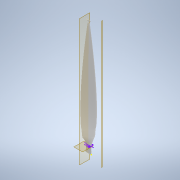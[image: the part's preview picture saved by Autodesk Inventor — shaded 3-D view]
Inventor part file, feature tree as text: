
AUTODESK INVENTOR PART (.ipt)
format: ipt  version: 2022 (Build 260153000, 153)  size: 1,145,856 bytes
history: native  units: mm
features: sketch x6, plane x3, loft x1, sweep x1
ambient origin geometry x8: Origin, YZ Plane, XZ Plane, XY Plane, X Axis, Y Axis, Z Axis, Center Point
bodies: Body1 (feature_tree)
feature tree (11):
  sketch  "Sketch1"  dims[d3=30.0mm d27=20.0mm]
  sketch  "Sketch2"  dims[d33=7.5mm d34=2.0mm]
  plane  "Work Plane1"
  sketch  "3D Sketch1"
  sketch  "Sketch4"  dims[d35=0.0mm d36=90.0deg]
  plane  "Work Plane2"
  sketch  "Sketch6"  dims[d37=0.0mm d38=90.0deg]
  loft  "Loft1"
  plane  "Work Plane3"
  sweep  "Sweep13"
  sketch  "Sketch7"  dims[d39=-7.5mm d42=20.0mm d43=7.5mm d44=310.0mm d45=0.0mm d46=0.0mm]
